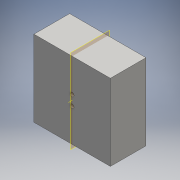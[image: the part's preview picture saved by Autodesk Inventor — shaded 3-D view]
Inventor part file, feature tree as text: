
AUTODESK INVENTOR PART (.ipt)
format: ipt  version: 2016 (Build 200138000, 138)  size: 131,584 bytes
history: native  units: mm
features: sketch x4, extrude x1, revolve x1, hole x1
ambient origin geometry x8: Origin, YZ Plane, XZ Plane, XY Plane, X Axis, Y Axis, Z Axis, Center Point
bodies: Solid1 (feature_tree)
feature tree (7):
  extrude  "Extrusion1"  Depth=30.0mm
  sketch  "Sketch2"  dims[d2=14.0mm d3=0.0mm d4=6.5mm]
  revolve  "Revolution1"  [1 undecoded]
  hole  "Hole1"  [1 undecoded]
  sketch  "Sketch1"  dims[d0=30.0mm d1=30.0mm]
  sketch  "Sketch3"  dims[d5=4.0mm d6=3.0mm]
  sketch  "Sketch4"  dims[d7=4.0mm d8=1.25mm d9=5.5mm d10=1.0mm d11=0.5mm d12=6.25mm d13=90.0deg d14=2.0mm d15=4.0mm d16=1.5mm d17=6.0mm d18=3.023mm d19=2.0mm d20=14.3117mm d21=100.0mm d22=20.594885mm]
note: 2 required parameter values undecoded (feature->parameter linkage not recoverable at this tier; creation-order binding heuristic only, values carry confidence <= 0.55)